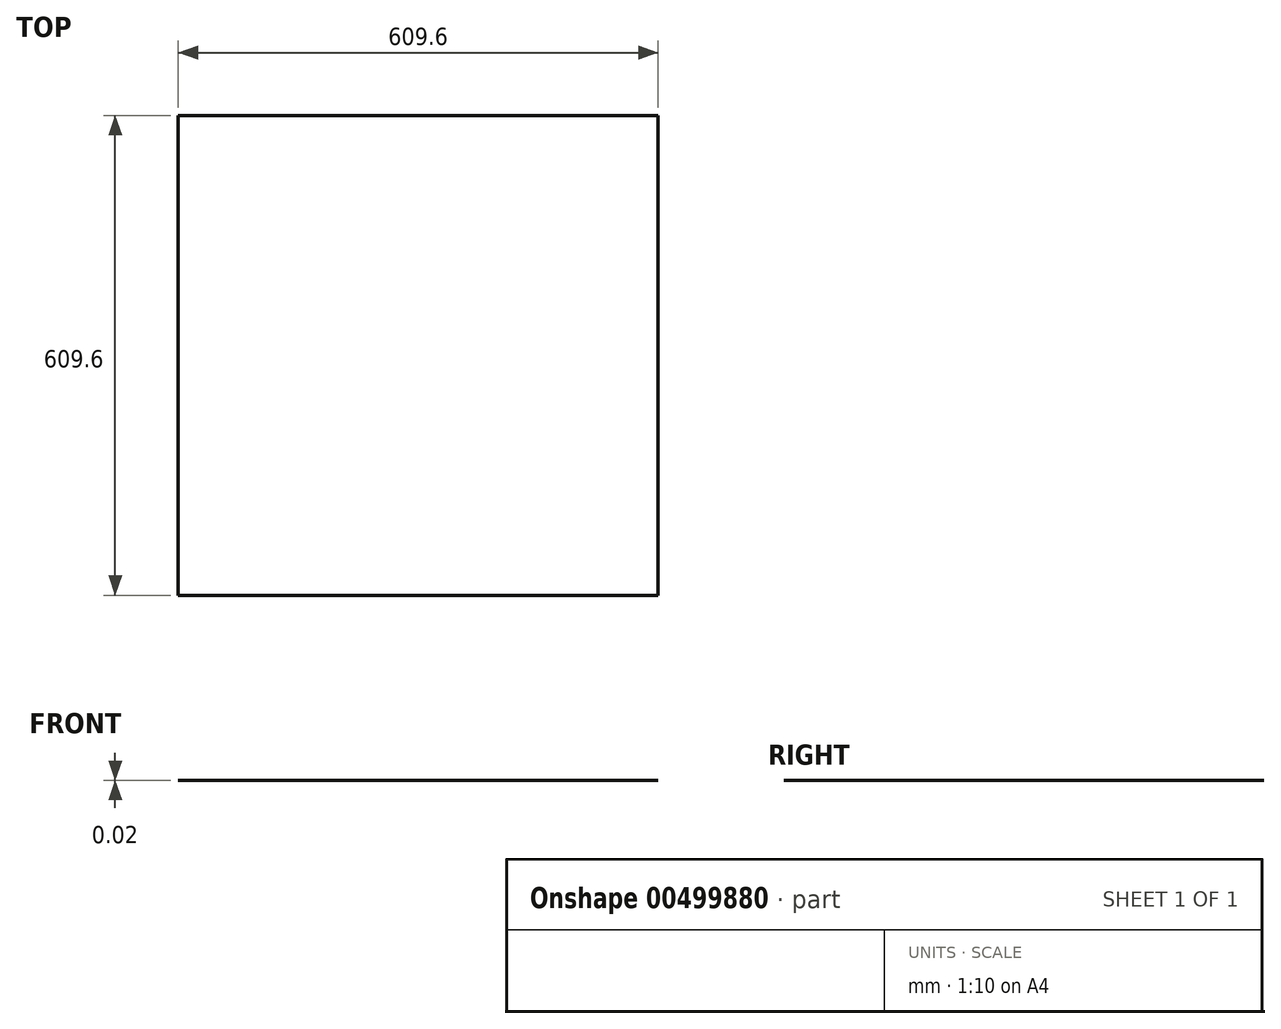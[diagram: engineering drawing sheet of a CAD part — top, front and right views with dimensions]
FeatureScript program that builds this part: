
annotation { "Feature Type Name" : "Feature", "Feature Type Description" : "" }
export const myFeature = defineFeature(function(context is Context, id is Id, definition is map)
    precondition{}
    {
        {
            var Q0;
            Q0=qCreatedBy(makeId("Top.planeOp"),FACE);
            var sketch = newSketch(context, id + "F0", { "sketchPlane" : qUnion([Q0])});
            skLineSegment(sketch, "E0.bottom", {"start": v(304.8, 304.8) * mm, "end": v(-304.8, 304.8) * mm});
            skLineSegment(sketch, "E0.top", {"start": v(304.8, -304.8) * mm, "end": v(-304.8, -304.8) * mm});
            skLineSegment(sketch, "E0.left", {"start": v(304.8, 304.8) * mm, "end": v(304.8, -304.8) * mm});
            skLineSegment(sketch, "E0.right", {"start": v(-304.8, 304.8) * mm, "end": v(-304.8, -304.8) * mm});
            skPoint(sketch, "E0.middle", {"position": v(0, 0) * mm});
            skSolve(sketch);
        }
        {
            var Q0;
            Q0 = qSketchRegion(id + "F0", true);
            extrude(context, id + "F1", {"entities" : qUnion([Q0]), "depth" : 7 / 406.4 * mm});
        }
    });
